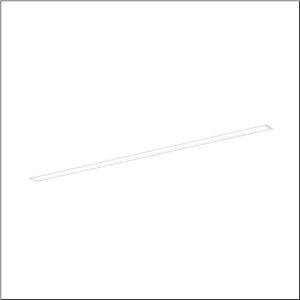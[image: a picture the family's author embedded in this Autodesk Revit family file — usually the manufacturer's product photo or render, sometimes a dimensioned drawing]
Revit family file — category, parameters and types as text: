
# Revit family: silica_r__21_51mx13tbt5w_c30f
name_source: partatom
category: Lighting Fixtures
units: mm (PartAtom-declared; Revit-internal decimal feet)

## family parameters
Cut with Voids When Loaded = No
Host = Face
Light Source = No
Part Type = Normal
Room Calculation Point = No
Round Connector Dimension = Use Diameter
Shared = No

## types (1)
- --- (1 x LED, 4030 lm, 40.5 W, 6500K)
    Apparent Load = 41 VA
    CIE Flux Codes = 78 96 99 100 100
    Color Rendering = 80
    Color Temperature = 6500K
    Default Elevation = 1800 mm
    Description = Silica® 21, office luminaire, primary optical cover: prismatic diffuser, of PMMA, CAT 2 (L<= 3000cd/m²), light emission: direct distribution, primary light characteristic: symmetric, installation type: recessed, LED, rated luminous flux: 4.030lm, luminous efficacy: 95lm/W, light colour: 8tw, colour temperature: 2700..6500K, with terminal, 3+2-pole, max. 2.5mm², mains connection: 220..240V, AC, 50/60Hz, rated input power: 42.6W, luminaire housing, of aluminium, traffic white (RAL 9016), length: 1.528mm, width: 79mm, height: 53mm, protection rating (complete): IP20, insulation class (complete): insulation class I (protective earthing), certification: CE, permissible operating ambient temperature: 0..+35°C, standard: EN 50419, packaging unit: 1 piece
    Height = 0 mm  [stored 0 ft]
    Lamp = 1 x LED
    Lamp Light Flux = 4030 lm
    Lamp Power = 40.5 W
    Lamp count = 1
    Length = 1527 mm
    Luminous efficacy = 100 lm/W
    Manufacturer = Siteco
    ModVariant = No
    Model = 51MX13TBT5W
    Mounting Place = Ceiling
    Mounting Type = Recessed
    Number of Poles = 1
    OnlyDefault = Yes
    Power Factor = 1
    Product Name = Silica® 21
    Product group = office luminaire | ceiling recessed
    ProductGroupID = 401
    Protection Class = Protection class I
    Protection Degree = IP 20
    RLX_Detail_Level = 1
    RLX_Emergency_Light_Flux = 0 lm
    RLX_Emergency_Type = 0
    RLX_Emergency_Type_DB = No
    RlxData = <blob elided: 10957 chars, md5=b35d6ae4>
    Socket = socket
    Standby Power = 0 W
    System Light Flux = 4030 lm
    System Power = 41 W
    Type Comments = individual setting
    Type Image = l_1251692.jpg
    URL = http://relux.com
    VarID = @adj_071173
    Voltage = 0 V
    Weight = 0.00 kg
    Width = 79 mm

note: [stored X ft] marks values corroborated as IEEE doubles in the binary element streams (Revit-internal decimal feet)

## geometry (parser evidence)
native form markers: Sweep x11
no freeform markers — native parametric forms only
